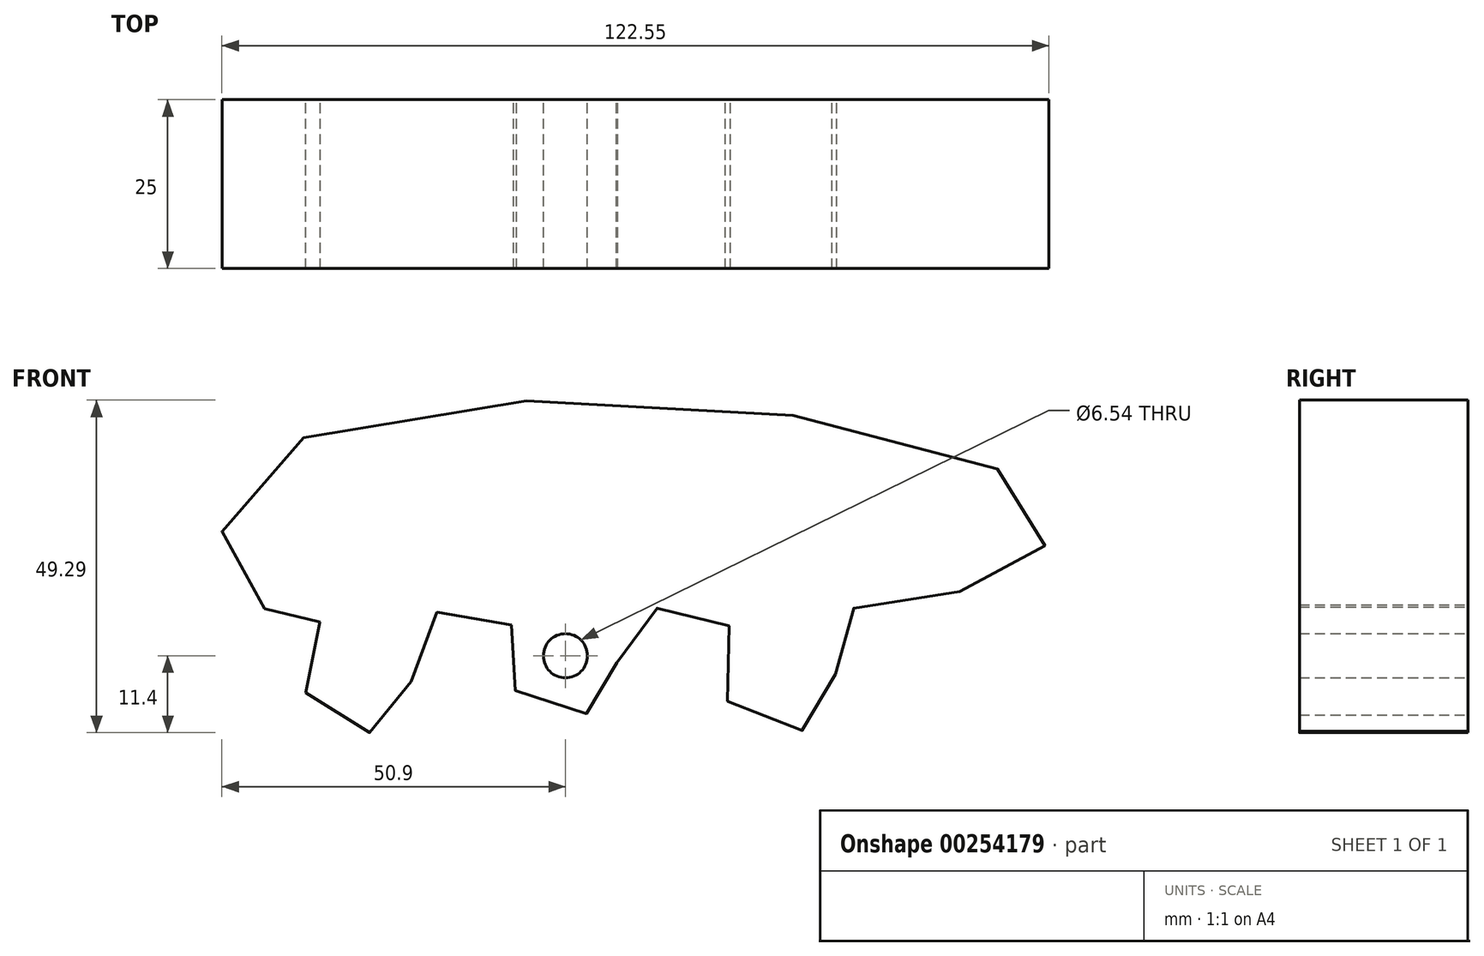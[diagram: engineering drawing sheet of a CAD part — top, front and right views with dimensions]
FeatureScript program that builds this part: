
annotation { "Feature Type Name" : "Feature", "Feature Type Description" : "" }
export const myFeature = defineFeature(function(context is Context, id is Id, definition is map)
    precondition{}
    {
        {
            var Q0;
            Q0=qCreatedBy(makeId("Front.planeOp"),FACE);
            var sketch = newSketch(context, id + "F0", { "sketchPlane" : qUnion([Q0])});
            skCircle(sketch, "E0", {"center": v(0, 0) * mm, "radius": 3.27 * mm});
            skFitSpline(sketch, "E1", {"points": [v(-7.97, 4.57) * mm, v(-6.9, -6.12) * mm, v(6.76, -6.84) * mm, v(8.54, 4.21) * mm, v(23.63, 5.64) * mm, v(24.46, -7.67) * mm, v(39.2, -9.1) * mm, v(40.26, 5.16) * mm, v(65.44, 11.34) * mm, v(69, 24.4) * mm, v(-45.98, 28.2) * mm, v(-45.5, 7.42) * mm, v(-36.48, 5.28) * mm, v(-38.02, -7.2) * mm, v(-24.48, -9.8) * mm, v(-21.27, 4.92) * mm, v(-7.97, 4.57) * mm]});
            skSolve(sketch);
        }
        {
            var Q0;
            Q0=makeQuery(id+"F0.imprint","IMPRINT",FACE,{"disambiguationData":[TD([[makeQuery(id+"F0.imprint","IMPRINT",EDGE,{"derivedFrom":sQuery(id+"F0.wireOp",EDGE,"E0")}),-1.0]])]});
            extrude(context, id + "F1", {"entities" : qUnion([Q0]), "depth" : 25 * mm});
        }
    });
